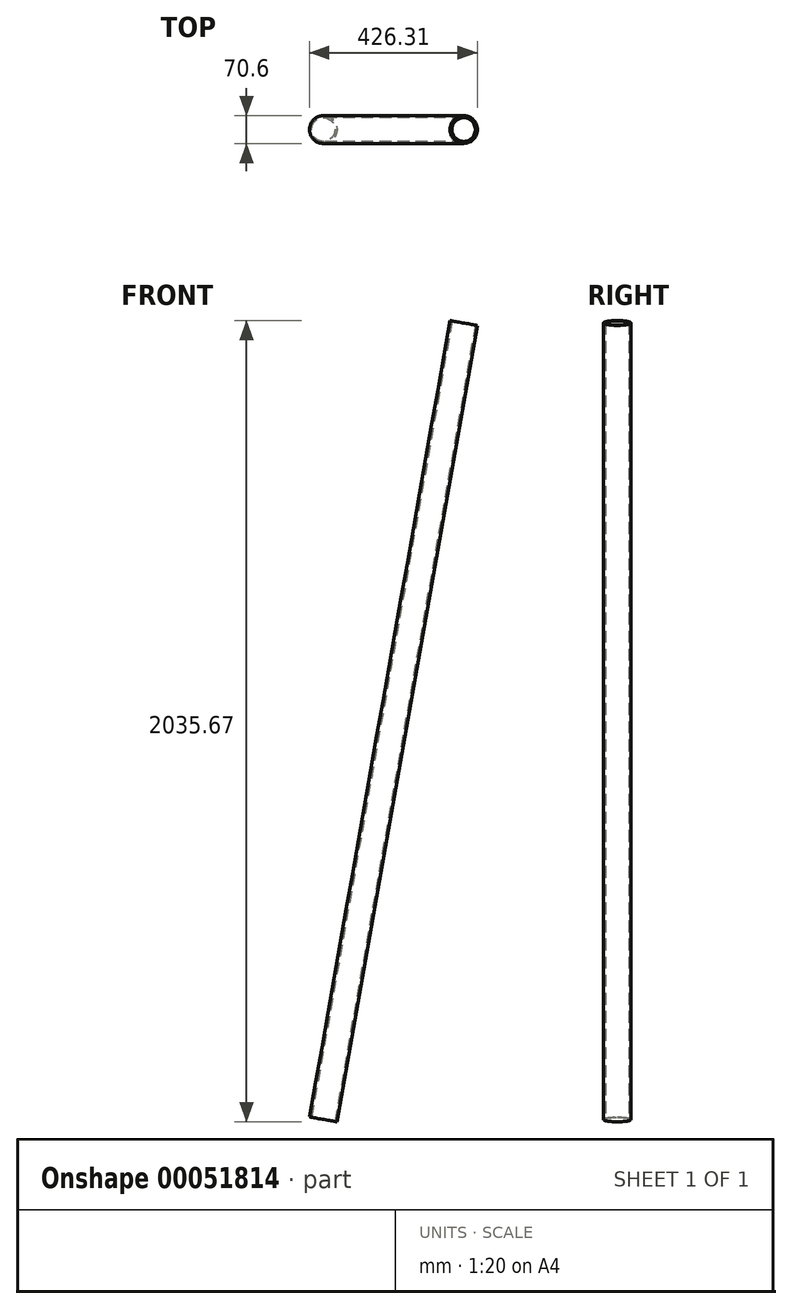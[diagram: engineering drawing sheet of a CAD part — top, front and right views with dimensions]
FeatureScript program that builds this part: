
annotation { "Feature Type Name" : "Feature", "Feature Type Description" : "" }
export const myFeature = defineFeature(function(context is Context, id is Id, definition is map)
    precondition{}
    {
        {
            var Q0;
            Q0=qCreatedBy(makeId("Front.planeOp"),FACE);
            var sketch = newSketch(context, id + "F0", { "sketchPlane" : qUnion([Q0])});
            skLineSegment(sketch, "E0.bottom", {"start": v(-600, -1100) * mm, "end": v(600, -1100) * mm, "construction": true});
            skLineSegment(sketch, "E0.top", {"start": v(-600, 1100) * mm, "end": v(600, 1100) * mm, "construction": true});
            skLineSegment(sketch, "E0.left", {"start": v(-600, -1100) * mm, "end": v(-600, 1100) * mm, "construction": true});
            skLineSegment(sketch, "E0.right", {"start": v(600, -1100) * mm, "end": v(600, 1100) * mm, "construction": true});
            skLineSegment(sketch, "E1", {"start": v(-499.22, -1054.05) * mm, "end": v(-142.44, 969.36) * mm, "construction": true});
            skLineSegment(sketch, "E2.0", {"start": v(-463.4, -1024.75) * mm, "end": v(-106.62, 998.6) * mm});
            skLineSegment(sketch, "E3.0", {"start": v(-458.38, -1025.7) * mm, "end": v(-101.6, 997.7) * mm});
            skLineSegment(sketch, "E4", {"start": v(-463.4, -1024.75) * mm, "end": v(-458.38, -1025.7) * mm});
            skLineSegment(sketch, "E5", {"start": v(-106.62, 998.6) * mm, "end": v(-101.6, 997.7) * mm});
            skLineSegment(sketch, "E6", {"start": v(0, 1100) * mm, "end": v(0, -1100) * mm, "construction": true});
            skPoint(sketch, "E7.MirrorCS.end.orphan", {"position": v(142.44, 969.36) * mm});
            skPoint(sketch, "E7.MirrorCS.start.orphan", {"position": v(499.22, -1054.05) * mm});
            skPoint(sketch, "E8.MirrorCS.end.orphan", {"position": v(101.6, 997.7) * mm});
            skPoint(sketch, "E8.MirrorCS.start.orphan", {"position": v(458.38, -1025.7) * mm});
            skSolve(sketch);
        }
        {
            var Q0;
            Q0 = qSketchRegion(id + "F0", true);
            var Q1;
            Q1=sQuery(id+"F0.wireOp",EDGE,"E1");
            revolve(context, id + "F1", {"entities" : qUnion([Q0]), "axis" : qUnion([Q1]), "revolveType" : RevolveType.FULL});
        }
    });
